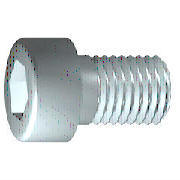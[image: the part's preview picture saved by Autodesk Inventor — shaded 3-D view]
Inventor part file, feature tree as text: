
AUTODESK INVENTOR PART (.ipt)
format: ipt  version: 2019 (Build 230136000, 136)  size: 192,000 bytes
history: native  units: mm (DEFAULTED — no unit token found)
features: sketch x2, extrude x1, plane x1, fillet x1
ambient origin geometry x7: Origin, YZ Plane, XY Plane, X Axis, Y Axis, Z Axis, Center Point
bodies: Solid1 (feature_tree), Body (feature_tree)
feature tree (5):
  extrude  "Slot"  Depth=6.0mm
  plane  "Work Plane1"
  fillet  "Fillet2"  Radius=6.0mm
  sketch  "Sketch1"  dims[d1=27.5mm d2=0.61355mm d3=6.0mm]
  sketch  "Sketch2"  dims[d4=3.0mm d5=60.0deg d6=6.0mm d7=6.0mm d8=5.773503mm d9=10.0mm d10=90.0deg d11=10.0mm d12=0.0mm d13=27.5mm d14=0.0mm d15=0.61345mm d16=0.61345mm d17=0.6mm d19=0.0mm d26=30.0mm d27=45.0deg d28=0.0mm d29=0.0mm d30=0.1mm]
